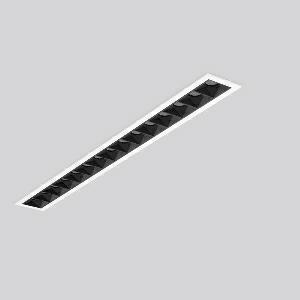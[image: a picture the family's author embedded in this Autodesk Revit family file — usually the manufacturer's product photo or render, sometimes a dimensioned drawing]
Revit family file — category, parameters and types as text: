
# Revit family: beamline_slim_641330_002_1_e22c
name_source: partatom
category: Lighting Fixtures
units: mm (PartAtom-declared; Revit-internal decimal feet)

## family parameters
Cut with Voids When Loaded = No
Host = Face
Light Source = No
Part Type = Normal
Room Calculation Point = No
Round Connector Dimension = Use Diameter
Shared = No

## types (1)
- BEAMLINE SLIM (1 x LED Modul 930, 3050 lm, 3000)
    Apparent Load = 36 VA
    CIE Flux Codes = 100 100 100 100 100
    Color Rendering = 90
    Color Temperature = 3000
    Default Elevation = 1800 mm
    Description = Series: BEAMLINE SLIM
Minimalistic recessed ceiling luminaire for aesthetically sophisticated lighting. Housing: metal, powder-coated. Perfect heat management with an aluminium heat sink. LED light unit with MRS technology: Mini-Reflector-System made of metallised thermoplastic with prismatic black glare-suppressing frame for pleasant glare-free light (RUG < 10). Medium beam light distribution. Ceiling installation with spring system. Including separate LED converter with connecting cable 450 mm. 
Colour: traffic white, matt (RAL 9016)
Length: 435 mm
Width: 45 mm
Height: 1.5 mm
Cut-out length: 430 mm
Cut-out width: 40 mm
Recess height: 110 mm
Luminaire: recess height: 60 mm
Lamp: LED
Socket: without socket
Colour temperature: 3000K
Colour rendering index (CRI): 90
System power: 36 W
Rated luminous flux: 3050 lm
Luminous efficiency: 85 lm/W
Control gear: Regulated power supply
Protection class: II
Type of protection: IP 20
    Height = 0 mm  [stored 0 ft]
    Lamp = 1 x LED Modul 930
    Lamp Light Flux = 3050 lm
    Lamp count = 1
    Length = 435 mm
    Lifetime = 50000 h
    Luminous efficacy = 85 lm/W
    Manufacturer = RZB
    ModVariant = No
    Model = 641330.002.1
    Mounting Place = Ceiling
    Mounting Type = Recessed
    Number of Poles = 1
    OnlyDefault = Yes
    Power Factor = 1
    Product Name = BEAMLINE SLIM
    Product group = Recessed LED linear luminaires
    ProductGroupID = 407
    Protection Class = Protection class II
    Protection Degree = IP 20
    RLX_Detail_Level = 1
    RLX_Emergency_Light_Flux = 0 lm
    RLX_Emergency_Type = 0
    RLX_Emergency_Type_DB = No
    RlxData = <blob elided: 18845 chars, md5=6f118f20>
    Socket = socket
    Standby Power = 0 W
    System Light Flux = 3050 lm
    System Power = 36 W
    Type Comments = Product without accessories
    Type Image = 641329.002.jpg
    URL = http://relux.com
    VarID = ---
    Voltage = 230 V
    Voltage Range = 220-240 V
    Weight = 0.00 kg
    Width = 45 mm

note: [stored X ft] marks values corroborated as IEEE doubles in the binary element streams (Revit-internal decimal feet)

## geometry (parser evidence)
native form markers: Blend x4, Sweep x10
no freeform markers — native parametric forms only
